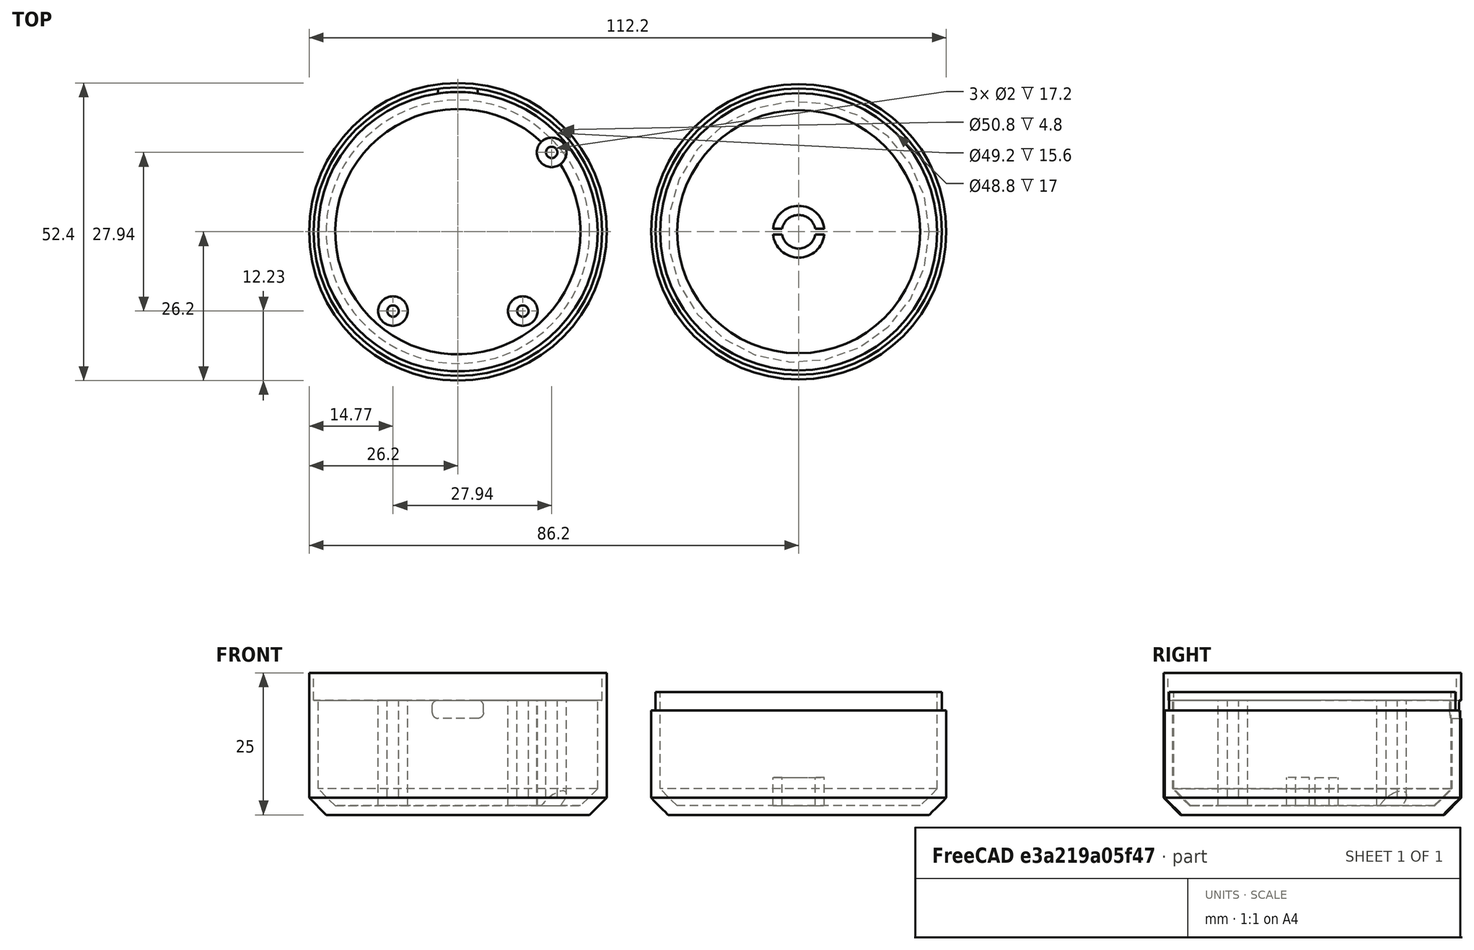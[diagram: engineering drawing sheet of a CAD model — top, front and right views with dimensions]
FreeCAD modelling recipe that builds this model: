
FCSTD DOCUMENT  (FreeCAD 0.16R)
Label: TinyNightLight
License: All rights reserved
LicenseURL: http://en.wikipedia.org/wiki/All_rights_reserved
objects: Part::Cylinder×14, Part::Cut×9, Part::Chamfer×4, Part::MultiFuse×3, Part::Box×2, Part::Fillet×1
note: 33 computed .brp shape members not serialized (recipe doc carries the construction recipe); baked Part::Feature solids carry a one-line shape summary decoded from their .brp

FEATURE [Part::Cylinder] Cylinder  label="Zylinder"
  Angle = 360
  Height = 25
  Radius = 26.2
FEATURE [Part::Cylinder] Cylinder001  label="Zylinder001"
  Angle = 360
  Height = 25
  Placement = pos=(0,0,1.6) rot=(0,0,1;0rad)
  Radius = 24.6
FEATURE [Part::Cylinder] Cylinder002  label="Zylinder002"
  Angle = 360
  Height = 25
  Placement = pos=(0,0,20.2) rot=(0,0,1;0rad)
  Radius = 25.4
FEATURE [Part::Cut] Cut
  Base = -> Cylinder
  Tool = -> Cylinder001
FEATURE [Part::Cut] Cut001
  Base = -> Cut
  Tool = -> Cylinder002
FEATURE [Part::Cylinder] Cylinder003  label="Zylinder003"
  Angle = 360
  Height = 20.2
  Placement = pos=(16.51,13.97,0) rot=(0,0,1;0rad)
  Radius = 2.6
FEATURE [Part::Chamfer] Chamfer
  Base = -> Cut001
  Edges = 1 edges r=3: [Edge9]
FEATURE [Part::Cylinder] Cylinder004  label="Zylinder004"
  Angle = 360
  Height = 20.2
  Placement = pos=(-11.43,-13.97,0) rot=(0,0,1;0rad)
  Radius = 2.6
FEATURE [Part::Cylinder] Cylinder005  label="Zylinder005"
  Angle = 360
  Height = 20.2
  Placement = pos=(11.43,-13.97,0) rot=(0,0,1;0rad)
  Radius = 2.6
FEATURE [Part::Cylinder] Cylinder006  label="Zylinder006"
  Angle = 360
  Height = 20.2
  Placement = pos=(16.51,13.97,3) rot=(0,0,1;0rad)
  Radius = 1
FEATURE [Part::Cut] Cut002
  Base = -> Cylinder003
  Tool = -> Cylinder006
FEATURE [Part::Cylinder] Cylinder007  label="Zylinder007"
  Angle = 360
  Height = 20.2
  Placement = pos=(-11.43,-13.97,3) rot=(0,0,1;0rad)
  Radius = 1
FEATURE [Part::Cut] Cut003
  Base = -> Cylinder004
  Tool = -> Cylinder007
FEATURE [Part::Cylinder] Cylinder008  label="Zylinder008"
  Angle = 360
  Height = 20.2
  Placement = pos=(11.43,-13.97,3) rot=(0,0,1;0rad)
  Radius = 1
FEATURE [Part::Cut] Cut004
  Base = -> Cylinder005
  Tool = -> Cylinder008
FEATURE [Part::MultiFuse] Fusion
  Shapes = -> [Chamfer,Cut003,Cut002,Cut004]
FEATURE [Part::Chamfer] Chamfer001  label="Bottom_raw"
  Base = -> Fusion
  Edges = 1 edges r=3: [Edge28]
FEATURE [Part::Box] Box  label="Würfel"
  Height = 3.2
  Length = 9
  Placement = pos=(-4.5,18,17) rot=(0,0,1;0rad)
  Width = 10
FEATURE [Part::Fillet] Fillet  label="USB"
  Base = -> Box
  Edges = 4 edges r=1: [Edge2,Edge4,Edge6,Edge8]
FEATURE [Part::Cut] Cut005  label="Bottom"
  Base = -> Chamfer001
  Tool = -> Fillet
FEATURE [Part::Cylinder] Cylinder009  label="Zylinder009"
  Angle = 360
  Height = 18.4
  Placement = pos=(60,0,0) rot=(0,0,1;0rad)
  Radius = 26
FEATURE [Part::Cylinder] Cylinder010  label="Zylinder010"
  Angle = 360
  Height = 21.6
  Placement = pos=(60,0,0) rot=(0,0,1;0rad)
  Radius = 25.2
FEATURE [Part::Cylinder] Cylinder011  label="Zylinder011"
  Angle = 360
  Height = 21.6
  Placement = pos=(60,0,1.6) rot=(0,0,1;0rad)
  Radius = 24.4
FEATURE [Part::MultiFuse] Fusion001
  Shapes = -> [Cylinder009,Cylinder010]
FEATURE [Part::Cut] Cut006
  Base = -> Fusion001
  Tool = -> Cylinder011
FEATURE [Part::Chamfer] Chamfer002
  Base = -> Cut006
  Edges = 1 edges r=3: [Edge10]
FEATURE [Part::Chamfer] Chamfer003
  Base = -> Chamfer002
  Edges = 1 edges r=3: [Edge11]
FEATURE [Part::Cylinder] Cylinder012  label="Zylinder012"
  Angle = 360
  Height = 5
  Placement = pos=(60,0,1.6) rot=(0,0,1;0rad)
  Radius = 4.55
FEATURE [Part::Cylinder] Cylinder013  label="Zylinder013"
  Angle = 360
  Height = 5
  Placement = pos=(60,0,1.6) rot=(0,0,1;0rad)
  Radius = 2.95
FEATURE [Part::Cut] Cut007
  Base = -> Cylinder012
  Tool = -> Cylinder013
FEATURE [Part::Box] Box001  label="Würfel001"
  Height = 10
  Length = 10
  Placement = pos=(55,-0.5,1.6) rot=(0,0,1;0rad)
  Width = 1
FEATURE [Part::Cut] Cut008
  Base = -> Cut007
  Tool = -> Box001
FEATURE [Part::MultiFuse] Fusion002  label="Top"
  Shapes = -> [Chamfer003,Cut008]
